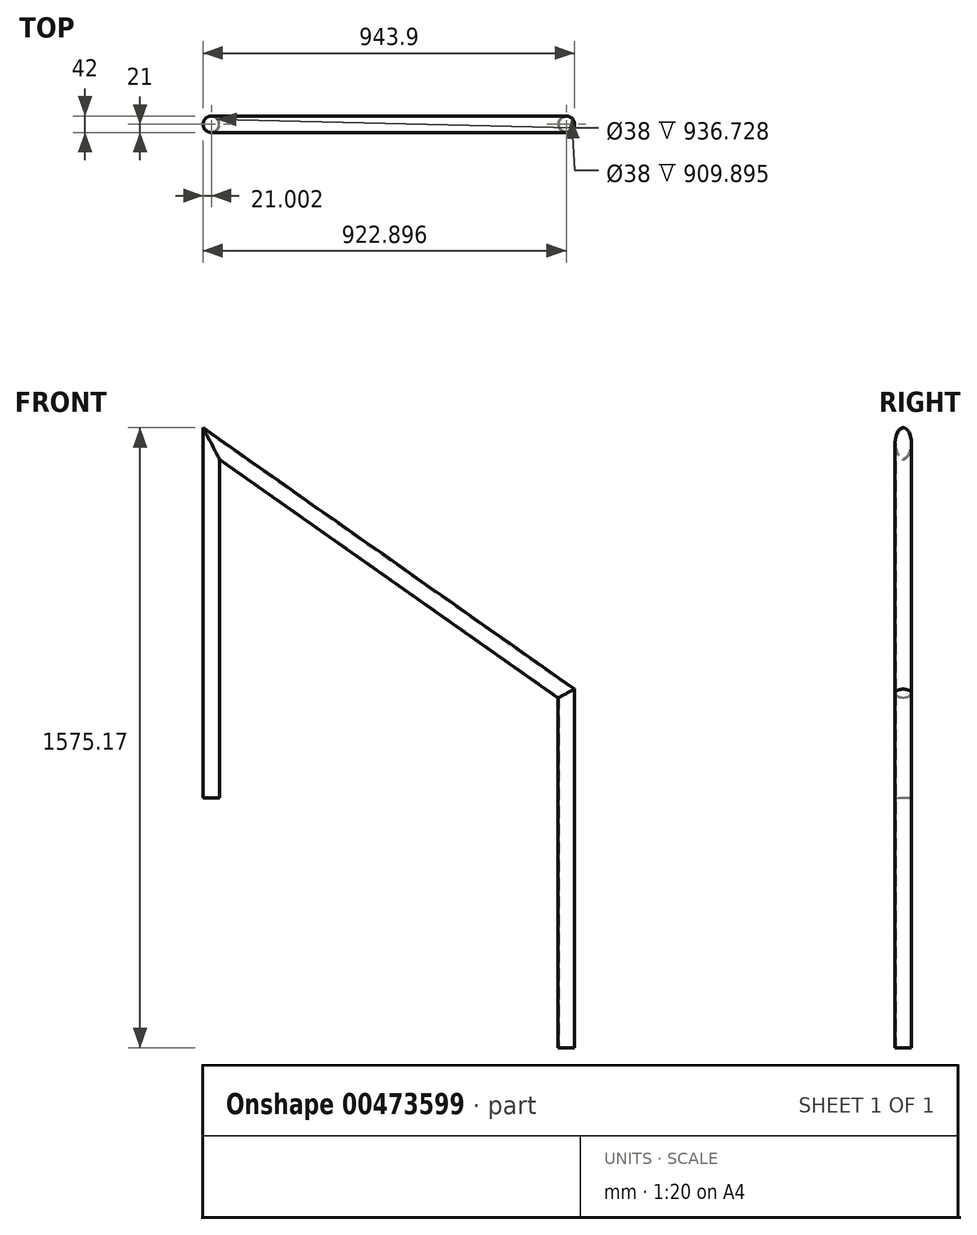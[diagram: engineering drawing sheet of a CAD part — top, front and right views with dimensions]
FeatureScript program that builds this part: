
annotation { "Feature Type Name" : "Feature", "Feature Type Description" : "" }
export const myFeature = defineFeature(function(context is Context, id is Id, definition is map)
    precondition{}
    {
        {
            var Q0;
            Q0=qCreatedBy(makeId("Front.planeOp"),FACE);
            var sketch = newSketch(context, id + "F0", { "sketchPlane" : qUnion([Q0])});
            skLineSegment(sketch, "E0", {"start": v(-451.75, -270.7) * mm, "end": v(-451.75, 629.3) * mm});
            skLineSegment(sketch, "E1", {"start": v(-451.75, 629.3) * mm, "end": v(450.15, -5.4) * mm});
            skLineSegment(sketch, "E2", {"start": v(450.15, -5.4) * mm, "end": v(450.15, -905.4) * mm});
            skLineSegment(sketch, "E3", {"start": v(-451.75, 482.57) * mm, "end": v(450.15, -152.14) * mm});
            skLineSegment(sketch, "E4", {"start": v(-451.75, -53.1) * mm, "end": v(450.15, -687.8) * mm});
            skSolve(sketch);
        }
        {
            var Q0;
            Q0=qCreatedBy(makeId("Top.planeOp"),FACE);
            var Q1;
            Q1=sQuery(id+"F0.wireOp",VERTEX,"E0.start");
            cPlane(context, id + "F1", {"entities" : qUnion([Q0, Q1]), "cplaneType" : CPlaneType.PLANE_POINT, "offset" : 25 * mm, "width" : 150 * mm, "height" : 150 * mm});
        }
        {
            var Q0;
            Q0=qCreatedBy(id+"F1.planeOp",FACE);
            var sketch = newSketch(context, id + "F2", { "sketchPlane" : qUnion([Q0])});
            skPoint(sketch, "E5.0", {"position": v(-451.75, 0) * mm});
            skCircle(sketch, "E6", {"center": v(-451.75, 0) * mm, "radius": 21 * mm});
            skSolve(sketch);
        }
        {
            var Q0;
            Q0=makeQuery(id+"F2.imprint","IMPRINT",FACE,{"disambiguationData":[TD([[makeQuery(id+"F2.imprint","IMPRINT",EDGE,{"derivedFrom":sQuery(id+"F2.wireOp",EDGE,"E6")}),1.0]])]});
            var Q1;
            Q1=sQuery(id+"F0.wireOp",EDGE,"E0");
            var Q2;
            Q2=sQuery(id+"F0.wireOp",EDGE,"E1");
            var Q3;
            Q3=sQuery(id+"F0.wireOp",EDGE,"E2");
            sweep(context, id + "F3", {"profiles" : qUnion([Q0]), "path" : qUnion([Q1, Q2, Q3])});
        }
        {
            var Q0;
            Q0=makeQuery(id+"F3.opSweep","CAP_FACE",FACE,{"disambiguationData":[OSD([sQuery(id+"F0.wireOp",VERTEX,"E2.end"),sQuery(id+"F2.wireOp",EDGE,"E6")])],"isStart":false});
            var Q1;
            Q1=makeQuery(id+"F3.opSweep","CAP_FACE",FACE,{"disambiguationData":[OSD([sQuery(id+"F0.wireOp",VERTEX,"E0.start"),sQuery(id+"F2.wireOp",EDGE,"E6")])],"isStart":true});
            var Q2;
            Q2=makeQuery(id+"F3.opSweep","SWEPT_BODY",BODY,{"disambiguationData":[OSD([sQuery(id+"F0.wireOp",EDGE,"E2"),sQuery(id+"F2.wireOp",EDGE,"E6")])]});
            shell(context, id + "F4", {"entities" : qUnion([Q0, Q1]), "parts" : qUnion([Q2]), "thickness" : 2 * mm});
        }
    });
